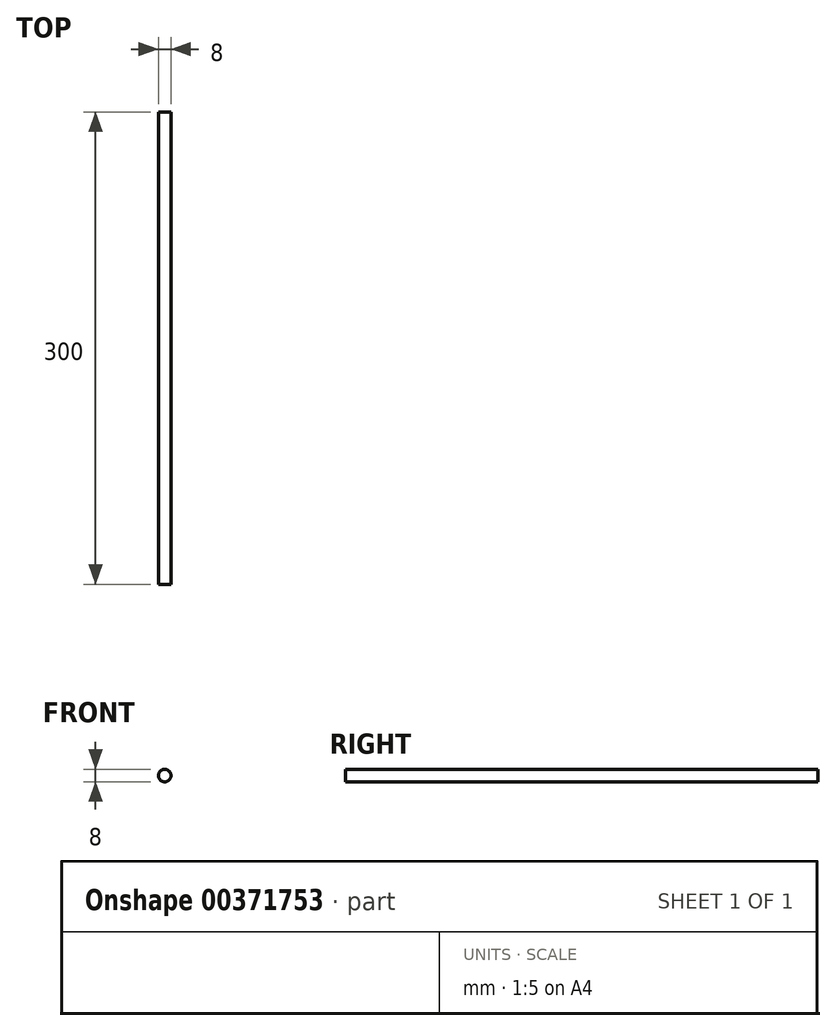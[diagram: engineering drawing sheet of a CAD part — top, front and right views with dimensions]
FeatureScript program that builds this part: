
annotation { "Feature Type Name" : "Feature", "Feature Type Description" : "" }
export const myFeature = defineFeature(function(context is Context, id is Id, definition is map)
    precondition{}
    {
        {
            var Q0;
            Q0=qCreatedBy(makeId("Front.planeOp"),FACE);
            var sketch = newSketch(context, id + "F0", { "sketchPlane" : qUnion([Q0])});
            skCircle(sketch, "E0", {"center": v(0, 0) * mm, "radius": 4 * mm});
            skSolve(sketch);
        }
        {
            assignVariable(context, id + "F1", {"name" : "x", "anyValue" : 300});
        }
        {
            var Q0;
            Q0=makeQuery(id+"F0.imprint","IMPRINT",FACE,{"disambiguationData":[TD([[makeQuery(id+"F0.imprint","IMPRINT",EDGE,{"derivedFrom":sQuery(id+"F0.wireOp",EDGE,"E0")}),1.0]])]});
            extrude(context, id + "F2", {"entities" : qUnion([Q0]), "depth" : (getVariable(context, 'x')) * mm});
        }
    });
